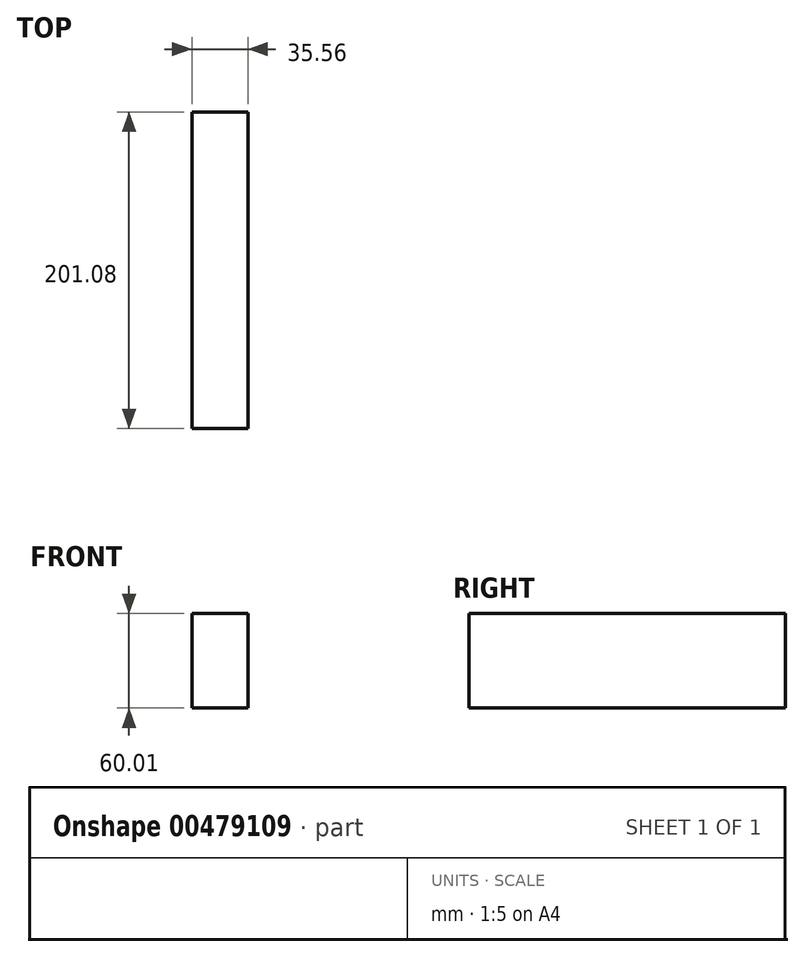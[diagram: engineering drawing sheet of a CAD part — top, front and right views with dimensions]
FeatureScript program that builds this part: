
annotation { "Feature Type Name" : "Feature", "Feature Type Description" : "" }
export const myFeature = defineFeature(function(context is Context, id is Id, definition is map)
    precondition{}
    {
        {
            var Q0;
            Q0=qCreatedBy(makeId("Right.planeOp"),FACE);
            var sketch = newSketch(context, id + "F0", { "sketchPlane" : qUnion([Q0])});
            skLineSegment(sketch, "E0.bottom", {"start": v(23.58, -20.52) * mm, "end": v(-177.5, -20.52) * mm});
            skLineSegment(sketch, "E0.top", {"start": v(23.58, 39.5) * mm, "end": v(-177.5, 39.5) * mm});
            skLineSegment(sketch, "E0.left", {"start": v(23.58, -20.52) * mm, "end": v(23.58, 39.5) * mm});
            skLineSegment(sketch, "E0.right", {"start": v(-177.5, -20.52) * mm, "end": v(-177.5, 39.5) * mm});
            skSolve(sketch);
        }
        {
            var Q0;
            Q0=makeQuery(id+"F0.imprint","IMPRINT",FACE,{"disambiguationData":[TD([[makeQuery(id+"F0.imprint","IMPRINT",EDGE,{"derivedFrom":sQuery(id+"F0.wireOp",EDGE,"E0.bottom")}),-1.0]])]});
            extrude(context, id + "F1", {"entities" : qUnion([Q0]), "depth" : 35.56 * mm});
        }
    });
